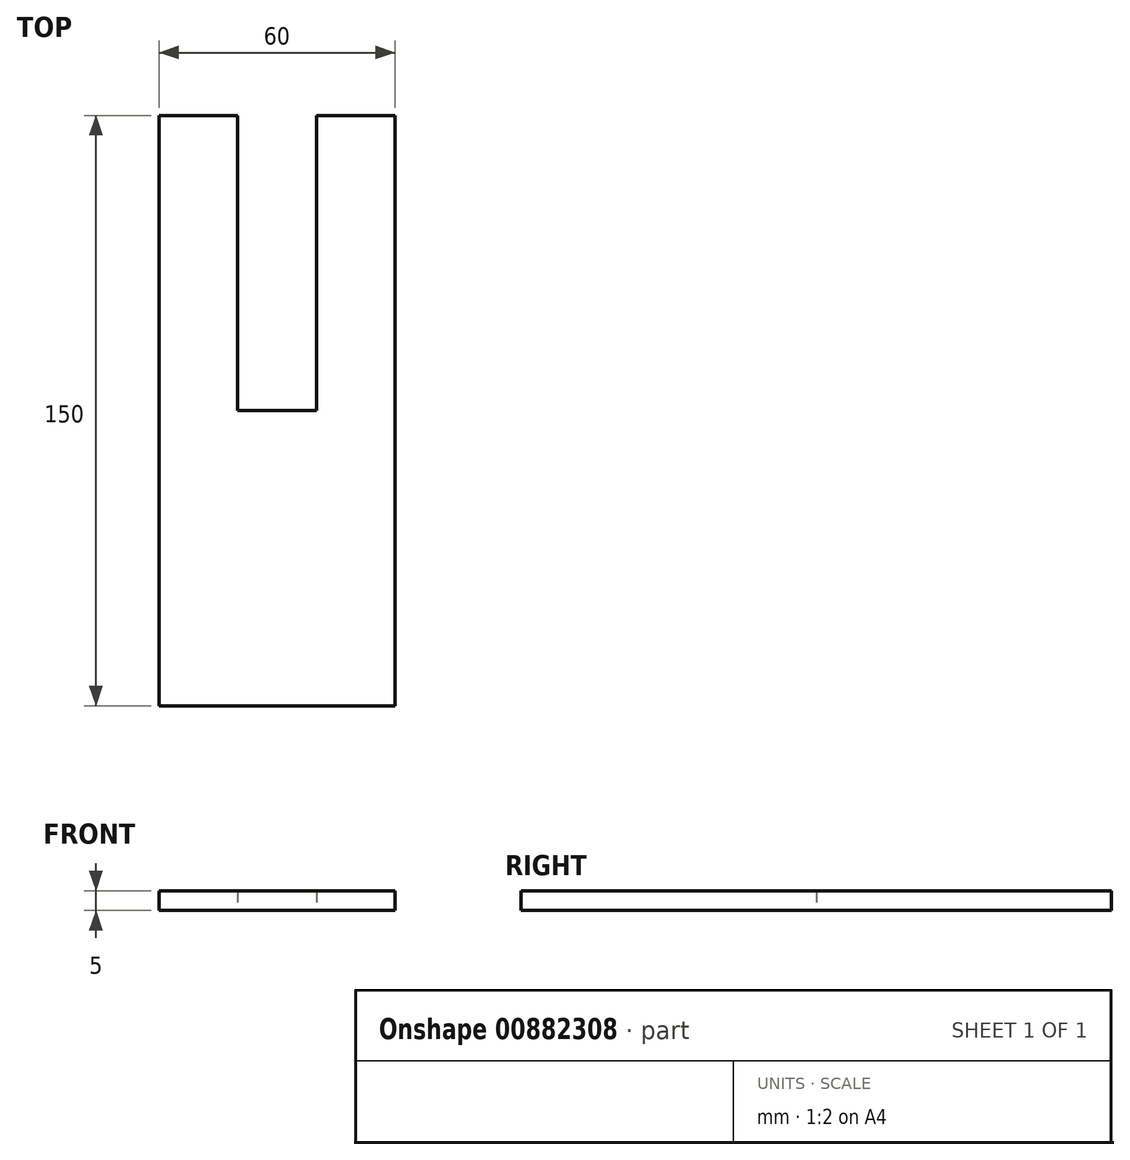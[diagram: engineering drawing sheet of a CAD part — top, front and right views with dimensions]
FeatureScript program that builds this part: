
annotation { "Feature Type Name" : "Feature", "Feature Type Description" : "" }
export const myFeature = defineFeature(function(context is Context, id is Id, definition is map)
    precondition{}
    {
        {
            var Q0;
            Q0=qCreatedBy(makeId("Top.planeOp"),FACE);
            var sketch = newSketch(context, id + "F0", { "sketchPlane" : qUnion([Q0])});
            skLineSegment(sketch, "E0", {"start": v(0, 0) * mm, "end": v(0, 150) * mm, "construction": true});
            skLineSegment(sketch, "E1", {"start": v(0, 150) * mm, "end": v(-10, 150) * mm, "construction": true});
            skLineSegment(sketch, "E2", {"start": v(-10, 150) * mm, "end": v(-30, 150) * mm});
            skLineSegment(sketch, "E3", {"start": v(-30, 150) * mm, "end": v(-30, 0) * mm});
            skLineSegment(sketch, "E4", {"start": v(-30, 0) * mm, "end": v(0, 0) * mm});
            skLineSegment(sketch, "E5", {"start": v(-10, 150) * mm, "end": v(-10, 75) * mm});
            skLineSegment(sketch, "E6", {"start": v(-10, 75) * mm, "end": v(0, 75) * mm});
            skLineSegment(sketch, "E7.MirrorCS", {"start": v(10, 75) * mm, "end": v(0, 75) * mm});
            skLineSegment(sketch, "E8.MirrorCS", {"start": v(10, 150) * mm, "end": v(10, 75) * mm});
            skLineSegment(sketch, "E9.MirrorCS", {"start": v(10, 150) * mm, "end": v(30, 150) * mm});
            skLineSegment(sketch, "E10.MirrorCS", {"start": v(30, 150) * mm, "end": v(30, 0) * mm});
            skLineSegment(sketch, "E11.MirrorCS", {"start": v(30, 0) * mm, "end": v(0, 0) * mm});
            skSolve(sketch);
        }
        {
            var Q0;
            Q0=qSketchRegion(id+"F0",true);
            extrude(context, id + "F1", {"entities" : qUnion([Q0]), "depth" : 5 * mm, "offsetDistance" : 25 * mm});
        }
    });
